# Revit family: 2058894 Feilo Sylvania Lighting Fixture MYRD IP FL 2-7K PHDMEM BLK WBEZ
name_source: partatom
category: Lighting Fixtures
revit_build: Autodesk Revit 2017 (Build: 20190507_1515(x64)
units: mm (PartAtom-declared; Revit-internal decimal feet)

## family parameters
Cut with Voids When Loaded = No
Host = Face
Light Source = Yes
OmniClass Number = 23.80.70.11.17
OmniClass Title = Specialized Lighting by Location or Use
Part Type = Normal
Room Calculation Point = No
Round Connector Dimension = Use Diameter
Shared = No

## types (1)
- 2058894 Feilo Sylvania Lighting Fixture MYRD IP FL 2-7K PHDMEM BLK WBEZ
    Accessory Diameter = 90 mm  [stored 0.295276 ft]
    Accessory Inner Diameter 1 = 88 mm  [stored 0.288714 ft]
    Accessory Inner Diameter 2 = 68 mm  [stored 0.223097 ft]
    Accessory Material = Aluminum_Sylvania_Myriad_White
    Apparent Load = 15 VA
    Assembly Code = D5020200
    AssetType = Fixed
    Body Material = Aluminum_Sylvania_Myriad_Gray
    Body Radius = 36.5 mm  [stored 0.119751 ft]
    Color Filter = 16777215
    Cost = 0 $
    Cutout Diameter = 75 mm
    Default Elevation = 0 mm  [stored 0 ft]
    Description = Supplied complete with electronic control gear Compact Fluorescent low energy downlight Emergency version passes through the cut out Ideal for low level orientation lighting New range of Architectural accessories each providing a different lit dimension New completely flush plaster up accessory ring for clean ceiling lines and smooth finish Order lamp separately
    Diffuser Diameter = 75 mm
    Diffuser Material = Glass_Sylvania_Myriad_Clear_4000K
    Dimming Lamp Color Temperature Shift = <None>
    DimmingControlOptions = Dimmable
    DocumentationLiterature = http://www.sylvania-lighting.com
    DurationUnit = hours
    ElectricShockClassification = Class II
    Emit Shape Visible in Rendering = No
    Emit from Circle Diameter = 68 mm  [stored 0.223097 ft]
    ExpectedLife = 50000
    Height = 72 mm
    IfcExportAs = IfcLightFixtureType
    IfcExportType = IfcLightFixtureType
    ImpactProtectionIndex = IK02
    IngressProtection = IP65
    InputNominalFrequency = 50/60 Hz
    InputVoltage = 230-240V~
    Keynote = 16500
    Keynote_2 = 16500
    Lamp = LED
    LampColourTemperature = 2700 K
    LampNominalLuminous = 889 lm
    LampsType = LED
    LightOutputRatio = 1
    LuminaireType = Ceiling recessed
    LuminousEfficacy = 57 lm/W
    Manufacturer = Feilo Sylvania
    ManufacturerName = Feilo Sylvania
    Material = Aluminium
    Model = MYRD IP FL 2.7K PHDMEM BLK WBEZ
    ModelNumber = 2058894
    ModelReference = MYRD IP FL 2.7K PHDMEM BLK WBEZ
    Name = MYRD IP FL 2.7K PHDMEM BLK WBEZ
    NominalHeight = 72 mm
    NominalLength = 76 mm
    NominalWidth = 0 mm  [stored 0 ft]
    PowerConsumption = 15 W
    PowerFactor = 0
    Recessed Depth = 72 mm
    Reflector Material = Aluminum_Sylvania_Myriad_Bright
    Reflector Radius = 35 mm
    Tilt Angle = -90°
    Type Image = <None>
    TypeName = MYRD IP FL 2.7K PHDMEM BLK WBEZ
    URL = http://www.sylvania-lighting.com
    Voltage = 230 V
    Weight = 1.44 kg

note: [stored X ft] marks values corroborated as IEEE doubles in the binary element streams (Revit-internal decimal feet)

## geometry (parser evidence)
native form markers: Sweep x2
no freeform markers — native parametric forms only
